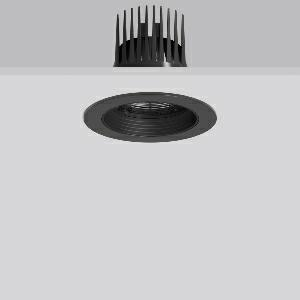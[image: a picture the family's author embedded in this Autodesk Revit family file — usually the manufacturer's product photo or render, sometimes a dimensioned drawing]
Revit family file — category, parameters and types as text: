
# Revit family: heledon_maxi_e_901762_003_76_a52a
name_source: partatom
category: Lighting Fixtures
units: mm (PartAtom-declared; Revit-internal decimal feet)

## family parameters
Cut with Voids When Loaded = No
Host = Face
Light Source = No
Part Type = Normal
Room Calculation Point = No
Round Connector Dimension = Use Diameter
Shared = No

## types (1)
- HELEDON maxi E (1 x LED Modul 930, 2800 lm, 3000)
    Apparent Load = 25 VA
    Approval mark = CE
    CIE Flux Codes = 96 100 100 100 100
    Color Rendering = 90
    Color Temperature = 3000
    Default Elevation = 1800 mm
    Description = Series: HELEDON maxi
Round recessed downlight. Housing: die-cast aluminium, powder-coated. Black plastic ring and recessed LED to prevent glare from the side. Optical assembly with lens made of plastic (polycarbonate) for the best homogeneous light distribution - can be changed without tools. Best colour rendering index Ra>90. Suitable for Recessed ceiling mounting. Installation without tools thanks to spring fastening system. Including separate LED converter with connecting cable 600 mm.High quality converter without flickering and stroboscopic effect. Through-wiring box (5 pole) available as accessory. The following accessories can be mounted without use of tools: interchangeable lenses, decorative glasses, honeycomb louvre, clear and frosted diffusers, white interchangeable plastic ring. 
Colour: deep black, matt (RAL 9005)
Diameter: 162 mm
Height: 3 mm
Cut-out diameter: 152 mm
Recess height: 200 mm
Luminaire: recess height: 135 mm
Lamp: LED
Socket: without socket
Colour temperature: 3000K
Colour rendering index (CRI): 92
System power: 25 W
Rated luminous flux: 2800 lm
Luminous efficiency: 112 lm/W
Control gear: Converter, dimmable, DALI
Protection class: II
Type of protection: IP 20
    Height = 0 mm  [stored 0 ft]
    Lamp = 1 x LED Modul 930
    Lamp Light Flux = 2800 lm
    Lamp count = 1
    Length = 162 mm
    Lifetime = 50000 h
    Luminous efficacy = 112 lm/W
    Manufacturer = RZB
    ModVariant = No
    Model = 901762.003.76
    Mounting Place = Ceiling
    Mounting Type = Recessed
    Number of Poles = 1
    OnlyDefault = Yes
    Power Factor = 1
    Product Name = HELEDON maxi E
    Product group = Recessed downlights
    ProductGroupID = 402
    Protection Class = Protection class II
    Protection Degree = IP 20
    RLX_Detail_Level = 1
    RLX_Emergency_Light_Flux = 0 lm
    RLX_Emergency_Type = 0
    RLX_Emergency_Type_DB = No
    RlxData = <blob elided: 121937 chars, md5=33ac4da6>
    Socket = socket
    Standby Power = 0 W
    System Light Flux = 2800 lm
    System Power = 25 W
    Type Comments = Product without accessories
    Type Image = 901663.003.jpg
    URL = http://relux.com
    VarID = ---
    Voltage = 230 V
    Voltage Range = 220-240 V
    Weight = 0.00 kg
    Width = 0 mm  [stored 0 ft]

note: [stored X ft] marks values corroborated as IEEE doubles in the binary element streams (Revit-internal decimal feet)

## geometry (parser evidence)
native form markers: Blend x4, Sweep x10
no freeform markers — native parametric forms only
